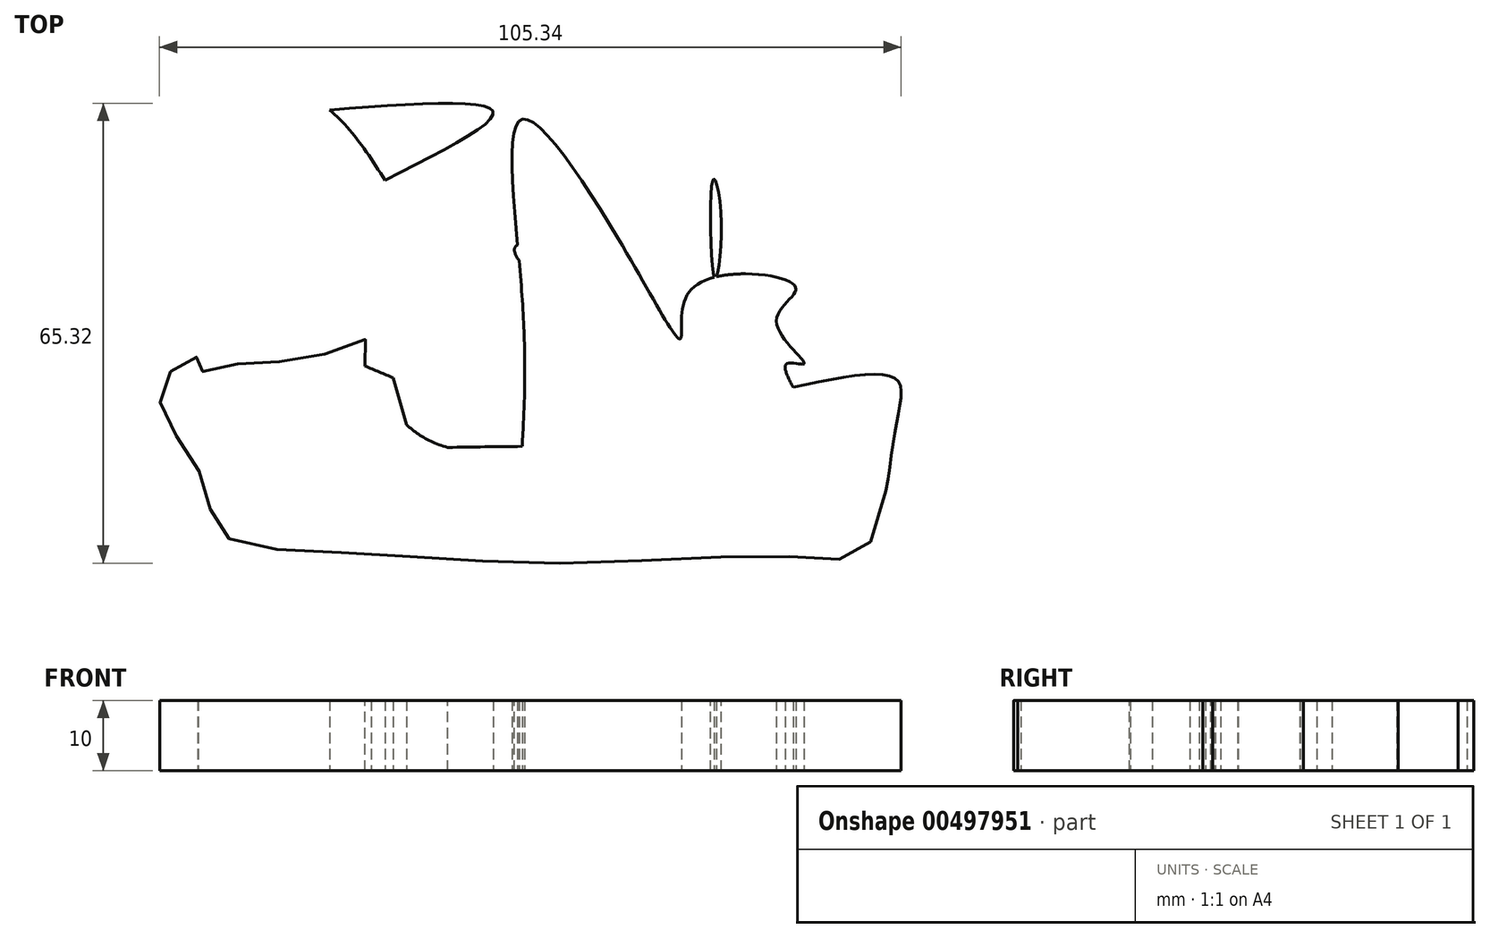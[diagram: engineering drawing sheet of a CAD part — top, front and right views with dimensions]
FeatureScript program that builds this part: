
annotation { "Feature Type Name" : "Feature", "Feature Type Description" : "" }
export const myFeature = defineFeature(function(context is Context, id is Id, definition is map)
    precondition{}
    {
        {
            var Q0;
            Q0=qCreatedBy(makeId("Top.planeOp"),FACE);
            var sketch = newSketch(context, id + "F0", { "sketchPlane" : qUnion([Q0])});
            skFitSpline(sketch, "E0", {"points": [v(-45.26, -42.65) * mm, v(-42.55, -50.19) * mm, v(-25.96, -52.9) * mm, v(4.8, -54.41) * mm, v(38.58, -53.5) * mm, v(48.83, -52.3) * mm, v(53.05, -35.4) * mm, v(53.05, -28.17) * mm, v(35.86, -29.98) * mm, v(18.97, -33.6) * mm, v(11.74, -36.62) * mm, v(-12.7, -37.22) * mm, v(-21.14, -31.19) * mm, v(-23.85, -31.19) * mm, v(-21.44, -23.04) * mm, v(-29.28, -25.16) * mm, v(-40.14, -26.06) * mm, v(-45.87, -26.97) * mm, v(-46.17, -25.16) * mm, v(-50.7, -28.17) * mm, v(-50.4, -34.2) * mm, v(-45.26, -42.65) * mm]});
            skFitSpline(sketch, "E1", {"points": [v(38.52, -29.43) * mm, v(37.67, -26.06) * mm, v(40.09, -26.06) * mm, v(36.17, -20.03) * mm, v(38.88, -15.2) * mm, v(24.4, -15.2) * mm, v(22.6, -22.44) * mm, v(15.96, -12.19) * mm, v(0, 8.62) * mm, v(0, -16.1) * mm, v(0, -38.68) * mm], "startDerivative": vector(-42.23, 81.85) * mm, "endDerivative": vector(-7.67, -135.75) * mm});
            skFitSpline(sketch, "E2", {"points": [v(0.42, -26.06) * mm, v(-14.2, -8.27) * mm, v(-29.28, 11.34) * mm, v(-35.91, 11.94) * mm, v(-35.31, 8.92) * mm, v(-35.31, 2.6) * mm, v(-32, 0) * mm, v(-30.18, 5) * mm, v(-34.7, 10.73) * mm], "startDerivative": vector(-73.36, 79.31) * mm, "endDerivative": vector(-53.95, 43.98) * mm});
            skFitSpline(sketch, "E3", {"points": [v(15.66, -20.63) * mm, v(-0.4, -11.4) * mm, v(0, -9.17) * mm, v(15.66, -20.63) * mm]});
            skFitSpline(sketch, "E4", {"points": [v(3.3, -36.62) * mm, v(3.3, -27.87) * mm, v(18.97, -26.97) * mm, v(37.67, -26.06) * mm], "startDerivative": vector(-9.98, 40.3) * mm, "endDerivative": vector(46.19, 4.75) * mm});
            skFitSpline(sketch, "E5", {"points": [v(27.34, -13.8) * mm, v(27.12, 0) * mm, v(28.32, -5.85) * mm, v(27.34, -13.8) * mm]});
            skFitSpline(sketch, "E6", {"points": [v(31.75, -13.31) * mm, v(31.75, 0) * mm], "startDerivative": vector(0, 13.31) * mm, "endDerivative": vector(0, 13.31) * mm});
            skFitSpline(sketch, "E7", {"points": [v(22.6, -22.44) * mm, v(36.17, -20.03) * mm], "startDerivative": vector(13.57, 2.41) * mm, "endDerivative": vector(13.57, 2.41) * mm});
            skFitSpline(sketch, "E8", {"points": [v(-41.64, -39.93) * mm, v(32.55, -38.68) * mm, v(-36.82, -41.74) * mm, v(-41.64, -39.93) * mm]});
            skLineSegment(sketch, "E9", {"start": v(-41.64, -44.16) * mm, "end": v(51.7, -44.16) * mm});
            skLineSegment(sketch, "E10", {"start": v(-27.47, 4.47) * mm, "end": v(-15.42, -38.1) * mm});
            skLineSegment(sketch, "E11", {"start": v(-32, 0) * mm, "end": v(-32, -25.16) * mm});
            skFitSpline(sketch, "E12", {"points": [v(-22.27, -26.42) * mm, v(-4.55, -31.19) * mm, v(-21.14, -4.04) * mm], "startDerivative": vector(56.03, -23.64) * mm, "endDerivative": vector(-49.1, 64.4) * mm});
            skFitSpline(sketch, "E13", {"points": [v(13.65, -8.27) * mm, v(22.3, -8.27) * mm], "startDerivative": vector(8.64, 0) * mm, "endDerivative": vector(8.64, 0) * mm});
            skFitSpline(sketch, "E14", {"points": [v(-19.42, 0) * mm, v(-4.07, 9.71) * mm, v(-27.3, 9.97) * mm], "startDerivative": vector(50.64, 25.42) * mm, "endDerivative": vector(-64.02, -4.82) * mm});
            skSolve(sketch);
        }
        {
            var Q0;
            Q0 = qSketchRegion(id + "F0", true);
            extrude(context, id + "F1", {"entities" : qUnion([Q0]), "depth" : 10 * mm});
        }
    });
